# Revit family: Geberit Bambini podna WC šolja za decu, dizajn lavlje šape, za WC sedište_PRO_450229
name_source: partatom
category: Plumbing Fixtures
revit_build: Autodesk Revit 2018 (Build: 20190510_1515(x64)
units: mm (PartAtom-declared; Revit-internal decimal feet)

## family parameters
Always vertical = Yes
Cut with Voids When Loaded = No
OmniClass Number = 23.45.05.21
OmniClass Title = Plumbing Fixtures - Sanitary Disposal Units
Part Type = Normal
Room Calculation Point = Yes
Round Connector Dimension = Use Diameter
Shared = No
Work Plane-Based = No

## types (1)
- 212000000 Geberit Bambini podna WC šolja za decu, dizajn lavlje šape, za WC sedište
    212000000_0_view = Yes
    BIM datoteka, datum izmene = 2020.05.18
    BIM datoteka, proizvođač = Geberit
    BIM datoteka, verzija = GEB MG 1.2
    Boja / površina = bela
    Broj artikla = 212000000
    CW Connection = Yes
    Description = Geberit Bambini podna WC šolja za decu, dizajn lavlje šape, za WC sedište
    EAN code basic data = 4022009021981
    GEB_culture = sr-RS
    GEB_generic_description = Bathroom collection
    GEB_generic_manufacturer = generic
    GEB_pimversion = 22.02.12
    GEB_processing_type = T
    GEB_reference = PRO_450229
    GEB_translations = {"ATT_10673":"EAN code basic data","ATT_10882":"Materijal proizvoda","ATT_459792":"Boja / površina","applicationPurposes":"Namene","application_range":"Oblast primene","brandName":"Robna marka","characteristics":"Svojstva","content_creator":"BIM datoteka, proizvođač","content_date_changed":"BIM datoteka, datum izmene","content_version":"BIM datoteka, verzija","key 1000":"Broj artikla","name":"Naziv","productBrand":"Robna marka proizvoda","scopeOfDelivery":"Obim isporuke","type":"Tip","fixed_material":"Osnovni materijal"}
    HW Connection = No
    IfcDescription = Geberit Bambini podna WC šolja za decu, dizajn lavlje šape, za WC sedište
    IfcExportAs = IfcSanitaryTerminal
    IfcExportType = TOILETPAN
    LOD300 = No
    LOD400 = Yes
    Manufacturer = Geberit
    Materijal proizvoda = sanitarna keramika
    Namene = Za decu
Za ustanove za brigu o deci
Za ugradne vodokotliće
Za nisko, poluvisoko i visoko montažni predzidni vodokotlić
    Naziv = Geberit Bambini podna WC šolja za decu, dizajn lavlje šape, za WC sedište
    Obim isporuke = WC šolja
    Oblast primene = Plumbing fixture
    Osnovni materijal = Geberit, Plastic, Opaque white
    Robna marka = Geberit
    Svojstva = Podni
Sa ispirnom ivicom
Tip 1, puno ispiranje 6 l, prema propisu EN 997
Horizontalni odvod
Sa pomoćnim sredstvom za penjanje
Sa nožicama u dizajnu lavlje šape
    Vent Connection = No
    Waste Connection = Yes
    outlet_flow = 0.0 L/s

## geometry (parser evidence)
native form markers: Blend x8, Sweep x10
no freeform markers — native parametric forms only
